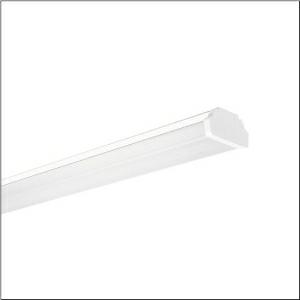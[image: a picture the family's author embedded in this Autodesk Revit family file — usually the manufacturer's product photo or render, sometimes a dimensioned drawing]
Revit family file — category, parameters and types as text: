
# Revit family: dus_r__31_gen_2_53bd812cv685c2_c333
name_source: partatom
category: Lighting Fixtures
units: mm (PartAtom-declared; Revit-internal decimal feet)

## family parameters
Cut with Voids When Loaded = No
Host = Face
Light Source = No
Part Type = Normal
Room Calculation Point = No
Round Connector Dimension = Use Diameter
Shared = No

## types (1)
- --- (1 x LED, 8970 lm, 49.9 W, 6500K)
    Apparent Load = 50 VA
    CIE Flux Codes = 47 80 95 93 100
    Color Rendering = 80
    Color Temperature = 6500K
    Default Elevation = 1800 mm
    Description = DUS® 31 Gen.2, luminaire insert, of sheet steel, coil coated, white, length: 1.535mm, width: 81mm, height: 90mm, 5x system unit, system units: 307mm, LED rated luminous flux: 8.970lm, light colour: 865, control gear: ON/OFF Multilumen, CLOi, with plug, 3-pole, with phase selection, mains connection: 220..240V, AC, 50/60Hz, start of lifetime: 50W, end of service life: 61W, through-wiring accessed according to module size, primary optical cover: cover, of PMMA, light emission: direct distribution, primary light characteristic: symmetric, protection rating (complete): IP20, protection rating (LED compartment): IP50, insulation class (complete): insulation class I (protective earthing), certification: CE, ENEC, VDE, UKCA, impact resistance: IK03, permissible ambient temperature for indoor applications: -35..+40°C, corresponds to IFS (International Featured Standards) requirements for safety and quality in the food industry, reducing of maximum allowable ambient temperature of 5°C with ceiling mounting, packaging unit: 1 piece
    Height = 95 mm
    Lamp = 1 x LED
    Lamp Light Flux = 8970 lm
    Lamp Power = 49.9 W
    Lamp count = 1
    Length = 1535 mm
    Luminous efficacy = 180 lm/W
    Manufacturer = Siteco
    ModVariant = No
    Model = 53BD812CV685C2
    Mounting Place = Ceiling
    Mounting Type = Pendant
    Number of Poles = 1
    OnlyDefault = Yes
    Power Factor = 1
    Product Name = DUS® 31 Gen.2
    Product group = luminaire insert
    ProductGroupID = 902
    Protection Class = Protection class I
    Protection Degree = IP 20
    RLX_Detail_Level = 1
    RLX_Emergency_Light_Flux = 0 lm
    RLX_Emergency_Type = 0
    RLX_Emergency_Type_DB = No
    RlxData = <blob elided: 29729 chars, md5=f000f489>
    Socket = socket
    Standby Power = 0 W
    System Light Flux = 8970 lm
    System Power = 50 W
    Type Comments = factory setting: luminous flux: 100 % | (A | C | E) | 116 mA
    Type Image = l_1319596.jpg
    URL = http://relux.com
    VarID = @adj_042244
    Voltage = 0 V
    Weight = 0.00 kg
    Width = 81 mm

## geometry (parser evidence)
native form markers: Blend x4, Sweep x13
no freeform markers — native parametric forms only
